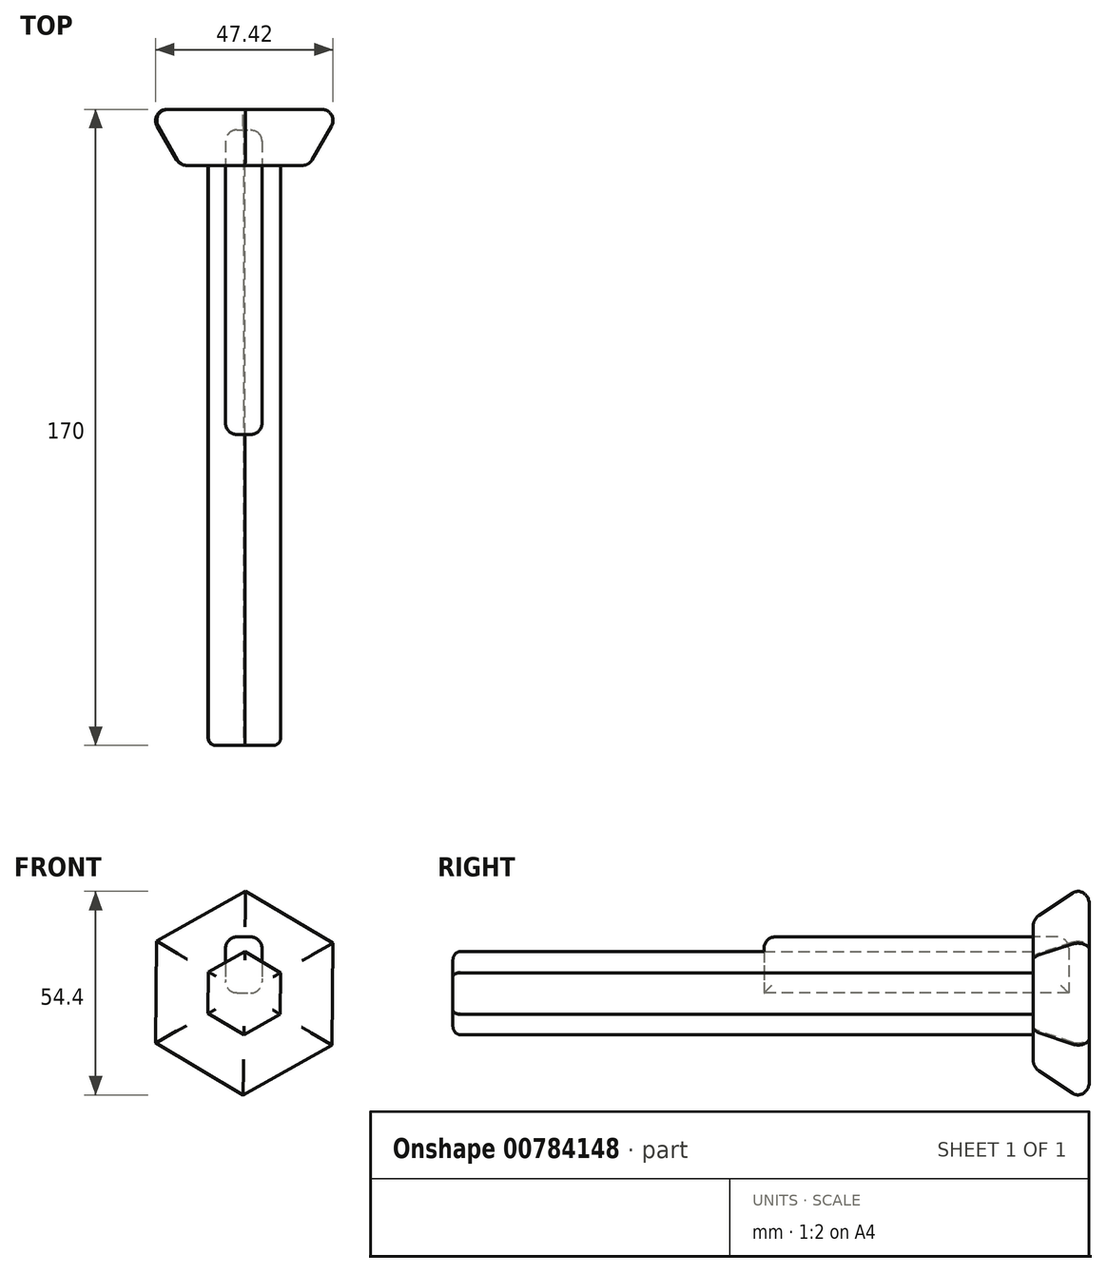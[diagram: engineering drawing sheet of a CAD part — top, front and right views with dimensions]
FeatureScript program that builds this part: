
annotation { "Feature Type Name" : "Feature", "Feature Type Description" : "" }
export const myFeature = defineFeature(function(context is Context, id is Id, definition is map)
    precondition{}
    {
        {
            var Q0;
            Q0=qCreatedBy(makeId("Front.planeOp"),FACE);
            var sketch = newSketch(context, id + "F0", { "sketchPlane" : qUnion([Q0])});
            skLineSegment(sketch, "E0.0", {"start": v(9.57, -5.67) * mm, "end": v(-0.13, -11.12) * mm});
            skLineSegment(sketch, "E0.1", {"start": v(-0.13, -11.12) * mm, "end": v(-9.7, -5.45) * mm});
            skLineSegment(sketch, "E0.2", {"start": v(-9.7, -5.45) * mm, "end": v(-9.57, 5.67) * mm});
            skLineSegment(sketch, "E0.3", {"start": v(-9.57, 5.67) * mm, "end": v(0.13, 11.12) * mm});
            skLineSegment(sketch, "E0.4", {"start": v(0.13, 11.12) * mm, "end": v(9.7, 5.45) * mm});
            skLineSegment(sketch, "E0.5", {"start": v(9.7, 5.45) * mm, "end": v(9.57, -5.67) * mm});
            skSolve(sketch);
        }
        {
            var Q0;
            Q0=makeQuery(id+"F0.imprint","IMPRINT",FACE,{"disambiguationData":[TD([[makeQuery(id+"F0.imprint","IMPRINT",EDGE,{"derivedFrom":sQuery(id+"F0.wireOp",EDGE,"E0.0")}),-1.0]])]});
            var Q1;
            Q1=sQuery(id+"F0.wireOp",EDGE,"E0.0");
            var Q2;
            Q2=sQuery(id+"F0.wireOp",EDGE,"E0.1");
            var Q3;
            Q3=sQuery(id+"F0.wireOp",EDGE,"E0.2");
            var Q4;
            Q4=sQuery(id+"F0.wireOp",EDGE,"E0.3");
            var Q5;
            Q5=sQuery(id+"F0.wireOp",EDGE,"E0.4");
            var Q6;
            Q6=sQuery(id+"F0.wireOp",EDGE,"E0.5");
            extrude(context, id + "F1", {"entities" : qUnion([Q0]), "surfaceEntities" : qUnion([Q1, Q2, Q3, Q4, Q5, Q6]), "depth" : 155 * mm, "offsetDistance" : 25 * mm, "symmetric" : true});
        }
        {
            var Q0;
            Q0=makeQuery(id+"F1.opExtrude","CAP_FACE",FACE,{"disambiguationData":[OSD([sQuery(id+"F0.wireOp",EDGE,"E0.0"),sQuery(id+"F0.wireOp",EDGE,"E0.1"),sQuery(id+"F0.wireOp",EDGE,"E0.2"),sQuery(id+"F0.wireOp",EDGE,"E0.3"),sQuery(id+"F0.wireOp",EDGE,"E0.4"),sQuery(id+"F0.wireOp",EDGE,"E0.5")])],"isStart":true});
            var sketch = newSketch(context, id + "F2", { "sketchPlane" : qUnion([Q0])});
            skCircle(sketch, "E1.cCircle", {"center": v(0, 0) * mm, "radius": 17.1 * mm, "construction": true});
            skLineSegment(sketch, "E1.0", {"start": v(17.2, -9.68) * mm, "end": v(0.22, -19.74) * mm});
            skLineSegment(sketch, "E1.1", {"start": v(0.22, -19.74) * mm, "end": v(-16.98, -10.06) * mm});
            skLineSegment(sketch, "E1.2", {"start": v(-16.98, -10.06) * mm, "end": v(-17.2, 9.68) * mm});
            skLineSegment(sketch, "E1.3", {"start": v(-17.2, 9.68) * mm, "end": v(-0.22, 19.74) * mm});
            skLineSegment(sketch, "E1.4", {"start": v(-0.22, 19.74) * mm, "end": v(16.98, 10.06) * mm});
            skLineSegment(sketch, "E1.5", {"start": v(16.98, 10.06) * mm, "end": v(17.2, -9.68) * mm});
            skPoint(sketch, "E1.0.midPoint", {"position": v(8.71, -14.7) * mm});
            skSolve(sketch);
        }
        {
            var Q0;
            Q0=makeQuery(id+"F2.imprint","IMPRINT",FACE,{"disambiguationData":[TD([[makeQuery(id+"F2.imprint","IMPRINT",EDGE,{"derivedFrom":sQuery(id+"F2.wireOp",EDGE,"E1.0")}),-1.0]])]});
            var Q1;
            Q1=makeQuery(id+"F2.imprint","IMPRINT",FACE,{"disambiguationData":[TD([[makeQuery(id+"F2.imprint","IMPRINT",EDGE,{"derivedFrom":makeQuery(id+"F1.opExtrude","CAP_EDGE",EDGE,{"disambiguationData":[OSD([sQuery(id+"F0.wireOp",EDGE,"E0.0")])],"isStart":true})}),1.0]])]});
            extrude(context, id + "F3", {"entities" : qUnion([Q0, Q1]), "depth" : 15 * mm, "offsetDistance" : 25 * mm, "hasDraft" : true, "draftAngle" : 30 * degree});
        }
        {
            var Q0;
            Q0=qCreatedBy(makeId("Top.planeOp"),FACE);
            var sketch = newSketch(context, id + "F4", { "sketchPlane" : qUnion([Q0])});
            skLineSegment(sketch, "E2.bottom", {"start": v(-5.02, 86.99) * mm, "end": v(4.7, 86.99) * mm});
            skLineSegment(sketch, "E2.top", {"start": v(-5.02, 5.6) * mm, "end": v(4.7, 5.6) * mm});
            skLineSegment(sketch, "E2.left", {"start": v(-5.02, 86.99) * mm, "end": v(-5.02, 5.6) * mm});
            skLineSegment(sketch, "E2.right", {"start": v(4.7, 86.99) * mm, "end": v(4.7, 5.6) * mm});
            skSolve(sketch);
        }
        {
            var Q0;
            Q0=qSketchRegion(id+"F4",true);
            extrude(context, id + "F5", {"entities" : qUnion([Q0]), "depth" : 15 * mm, "offsetDistance" : 25 * mm});
        }
        {
            var Q0;
            Q0=makeQuery(id+"F5.opExtrude","CAP_FACE",FACE,{"disambiguationData":[OSD([sQuery(id+"F4.wireOp",EDGE,"E2.bottom"),sQuery(id+"F4.wireOp",EDGE,"E2.top"),sQuery(id+"F4.wireOp",EDGE,"E2.left"),sQuery(id+"F4.wireOp",EDGE,"E2.right")])],"isStart":false});
            var Q1;
            Q1=makeQuery(id+"F5.opExtrude","SWEPT_FACE",FACE,{"disambiguationData":[OSD([sQuery(id+"F4.wireOp",EDGE,"E2.right")])]});
            var Q2;
            Q2=makeQuery(id+"F5.opExtrude","SWEPT_FACE",FACE,{"disambiguationData":[OSD([sQuery(id+"F4.wireOp",EDGE,"E2.left")])]});
            var Q3;
            Q3=makeQuery(id+"F5.opExtrude","CAP_EDGE",EDGE,{"disambiguationData":[OSD([sQuery(id+"F4.wireOp",EDGE,"E2.right")])],"isStart":false});
            var Q4;
            Q4=makeQuery(id+"F5.opExtrude","CAP_EDGE",EDGE,{"disambiguationData":[OSD([sQuery(id+"F4.wireOp",EDGE,"E2.left")])],"isStart":false});
            var Q5;
            Q5=makeQuery(id+"F3.opExtrude","CAP_FACE",FACE,{"disambiguationData":[OSD([sQuery(id+"F2.wireOp",EDGE,"E1.0"),sQuery(id+"F2.wireOp",EDGE,"E1.1"),sQuery(id+"F2.wireOp",EDGE,"E1.2"),sQuery(id+"F2.wireOp",EDGE,"E1.3"),sQuery(id+"F2.wireOp",EDGE,"E1.4"),sQuery(id+"F2.wireOp",EDGE,"E1.5")])],"isStart":false});
            var Q6;
            Q6=makeQuery(id+"F3.opExtrude","CAP_FACE",FACE,{"disambiguationData":[OSD([sQuery(id+"F2.wireOp",EDGE,"E1.0"),sQuery(id+"F2.wireOp",EDGE,"E1.1"),sQuery(id+"F2.wireOp",EDGE,"E1.2"),sQuery(id+"F2.wireOp",EDGE,"E1.3"),sQuery(id+"F2.wireOp",EDGE,"E1.4"),sQuery(id+"F2.wireOp",EDGE,"E1.5")])],"isStart":true});
            fillet(context, id + "F6", {"entities" : qUnion([Q0, Q1, Q2, Q3, Q4, Q5, Q6]), "radius" : 3 * mm, "tangentPropagation" : true, "allowEdgeOverflow" : false});
        }
        {
            var Q0;
            Q0=makeQuery(id+"F1.opExtrude","CAP_FACE",FACE,{"disambiguationData":[OSD([sQuery(id+"F0.wireOp",EDGE,"E0.0"),sQuery(id+"F0.wireOp",EDGE,"E0.1"),sQuery(id+"F0.wireOp",EDGE,"E0.2"),sQuery(id+"F0.wireOp",EDGE,"E0.3"),sQuery(id+"F0.wireOp",EDGE,"E0.4"),sQuery(id+"F0.wireOp",EDGE,"E0.5")])],"isStart":false});
            fillet(context, id + "F7", {"entities" : qUnion([Q0]), "radius" : 2 * mm, "tangentPropagation" : true, "allowEdgeOverflow" : false});
        }
    });
